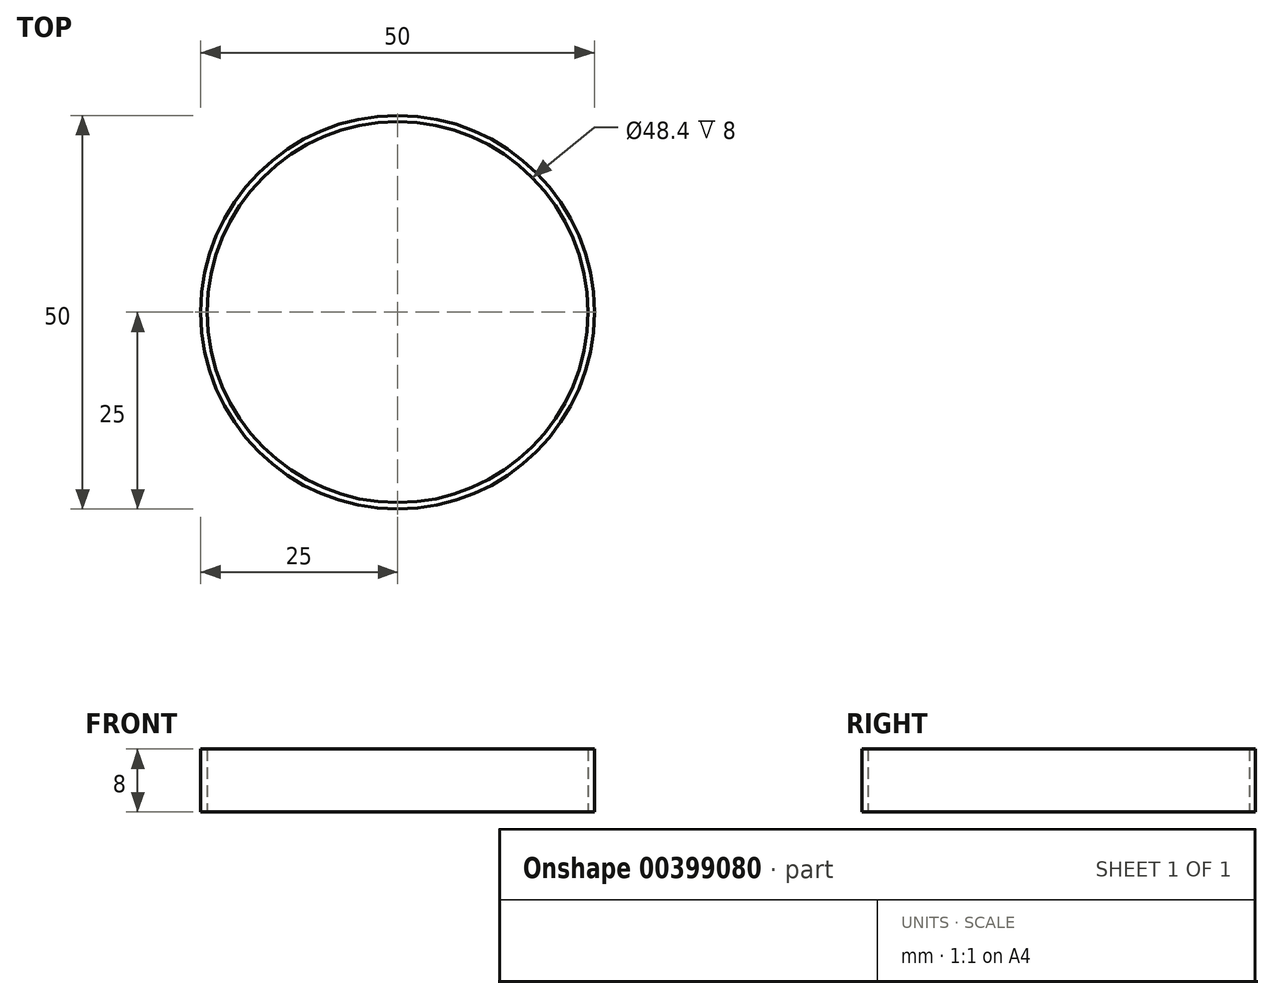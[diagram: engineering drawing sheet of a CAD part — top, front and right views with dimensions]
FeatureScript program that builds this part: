
annotation { "Feature Type Name" : "Feature", "Feature Type Description" : "" }
export const myFeature = defineFeature(function(context is Context, id is Id, definition is map)
    precondition{}
    {
        {
            var Q0;
            Q0=qCreatedBy(makeId("Top.planeOp"),FACE);
            var sketch = newSketch(context, id + "F0", { "sketchPlane" : qUnion([Q0])});
            skCircle(sketch, "E0", {"center": v(0, 0) * mm, "radius": 25 * mm});
            skCircle(sketch, "E1", {"center": v(0, 0) * mm, "radius": 24.2 * mm});
            skSolve(sketch);
        }
        {
            var Q0;
            Q0=makeQuery(id+"F0.imprint","IMPRINT",FACE,{"disambiguationData":[TD([[makeQuery(id+"F0.imprint","IMPRINT",EDGE,{"derivedFrom":sQuery(id+"F0.wireOp",EDGE,"E0")}),1.0]])]});
            extrude(context, id + "F1", {"entities" : qUnion([Q0]), "depth" : 8 * mm});
        }
    });
